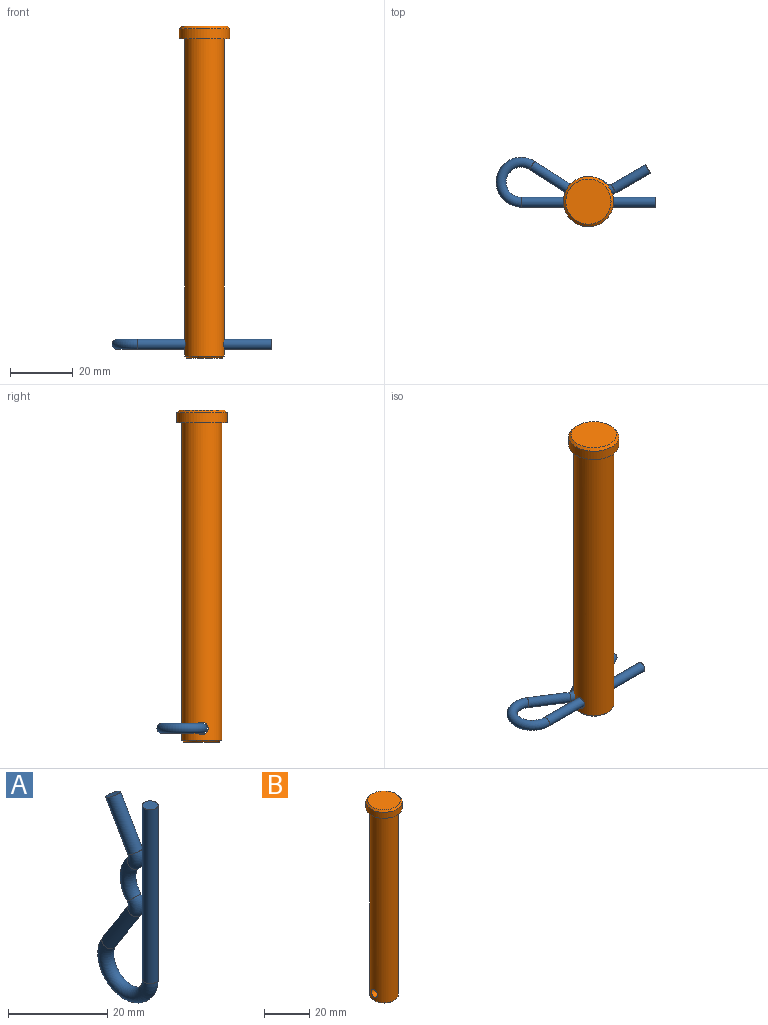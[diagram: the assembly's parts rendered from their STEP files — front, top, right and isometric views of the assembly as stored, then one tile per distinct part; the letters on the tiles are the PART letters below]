
ASSEMBLY  parts=2 mates=1
PART A: 9 faces, bbox 3.2x17.2x51.5 mm
  f0: torus R=6.35mm, axis (1,0,0), area 235mm2, adj f4,f5
  f1: torus R=2.38mm, axis (-1,0,0), area 31.5mm2, adj f2,f5
  f2: torus R=6.35mm, axis (1,0,0), area 95.8mm2, adj f1,f3
  f3: torus R=2.38mm, axis (-1,0,0), area 30.4mm2, adj f2,f6
  f4: cylinder r=1.59mm len=42.86mm, axis (0,0,1), area 427.5mm2, adj f0,f8
  f5: cylinder r=1.59mm len=13.24mm, axis (0,-0.54,0.84), area 136.5mm2, adj f0,f1
  f6: cylinder r=1.59mm len=12.5mm, axis (0,0.5,0.87), area 125.7mm2, adj f3,f7
  f7: plane 3.18x2.75mm, normal (0,0.5,0.87), area 7.9mm2, adj f6
  f8: plane 3.18x3.18mm, normal (0,0,1), area 7.9mm2, adj f4
PART B: 8 faces, bbox 16x16x105.7 mm
  f0: cone r=6.35mm half-angle=45deg, axis (0,0,1), area 34mm2, adj f4,f5
  f1: cylinder r=1.98mm len=12.7mm, axis (1,0,0), area 158.3mm2, adj f4
  f2: cone r=7.19mm half-angle=45deg, axis (0,0,-1), area 54.9mm2, adj f3,f7
  f3: cylinder r=8mm len=16mm, axis (0,0,-1), area 163.4mm2, adj f2,f6
  f4: cylinder r=6.35mm len=100.97mm, axis (0,0,-1), area 4003.3mm2, adj f0,f1,f6
  f5: plane 11.43x11.43mm, normal (0,0,-1), area 102.6mm2, adj f0
  f6: plane 16x16mm, normal (0,0,-1), area 74.4mm2, adj f3,f4
  f7: plane 14.38x14.38mm, normal (0,0,1), area 162.3mm2, adj f2
PLACE A rot(axis=(0,1,0),90deg) t=(21.43,0,-101.3)mm
PLACE B t=(0,0,-54.86)mm
MATE fastened A.f4 <-> B.f1  axis (1,0,0) through (0,0,-101.3)mm
